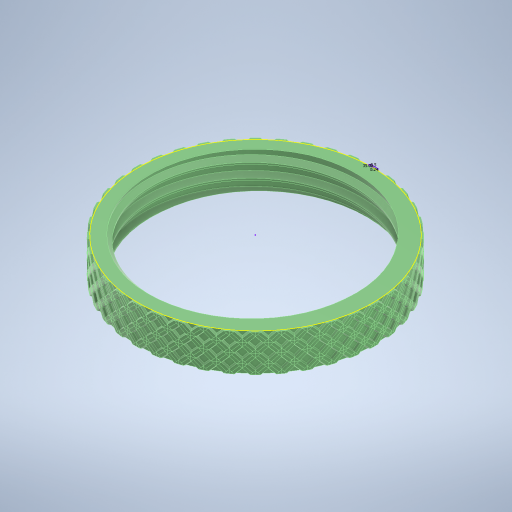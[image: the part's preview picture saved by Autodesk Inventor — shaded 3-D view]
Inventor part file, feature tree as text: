
AUTODESK INVENTOR PART (.ipt)
format: ipt  version: 2024.1 (Build 281209000, 209)  size: 5,693,952 bytes
history: native  units: mm
features: sketch x3, helix x3, extrude x1, draft x1, direct_edit x1, pattern_circular x1, other x1
ambient origin geometry x8: Origin, YZ Plane, XZ Plane, XY Plane, X Axis, Y Axis, Z Axis, Center Point
bodies: Solid1 (feature_tree)
feature tree (11):
  sketch  "Sketch1"  dims[d0=6.806784mm d1=0.55605mm d2=6.806784mm d3=0.6mm d4=12.875mm d5=12.5mm d6=1.047198mm d7=0.896783mm d8=2.25mm]
  extrude  "Extrusion1"  Depth=12.5mm
  draft  "FaceDraft1"
  helix  "Coil1"  [1 undecoded]
  direct_edit  "Direct Edit1"
  sketch  "Sketch3"  dims[d11=29.5mm d12=26.793566mm d13=14.75mm d14=13.899631mm d15=1.290245mm d16=12.875mm d17=0.0mm d18=12.875mm d19=26.794mm d20=2.5mm d21=5.0mm d22=0.0mm d23=1.047198mm d24=2.0mm d25=10.0mm d26=70.0mm d27=-1.047198mm d28=90.0deg d29=90.0deg d30=0.0mm d31=0.0mm d32=-0.25mm d33=0.24mm d34=6.108652mm d35=0.5mm d36=100.0mm d37=5.0mm d38=70.0mm d39=0.0mm d40=90.0deg d41=90.0deg d42=0.0mm d43=0.0mm d44=100.0mm d45=5.0mm d46=70.0mm d47=0.0mm d48=90.0deg d49=90.0deg d50=0.0mm d51=0.0mm d52=400.0mm d53=360.0deg]
  helix  "Coil2"  [1 undecoded]
  helix  "Coil3"  [1 undecoded]
  pattern_circular  "Circular Pattern1"  [2 undecoded]
  sketch  "Sketch2"  dims[d9=90.0deg]
  other  "Size1"
note: 5 required parameter values undecoded (feature->parameter linkage not recoverable at this tier; creation-order binding heuristic only, values carry confidence <= 0.55)
